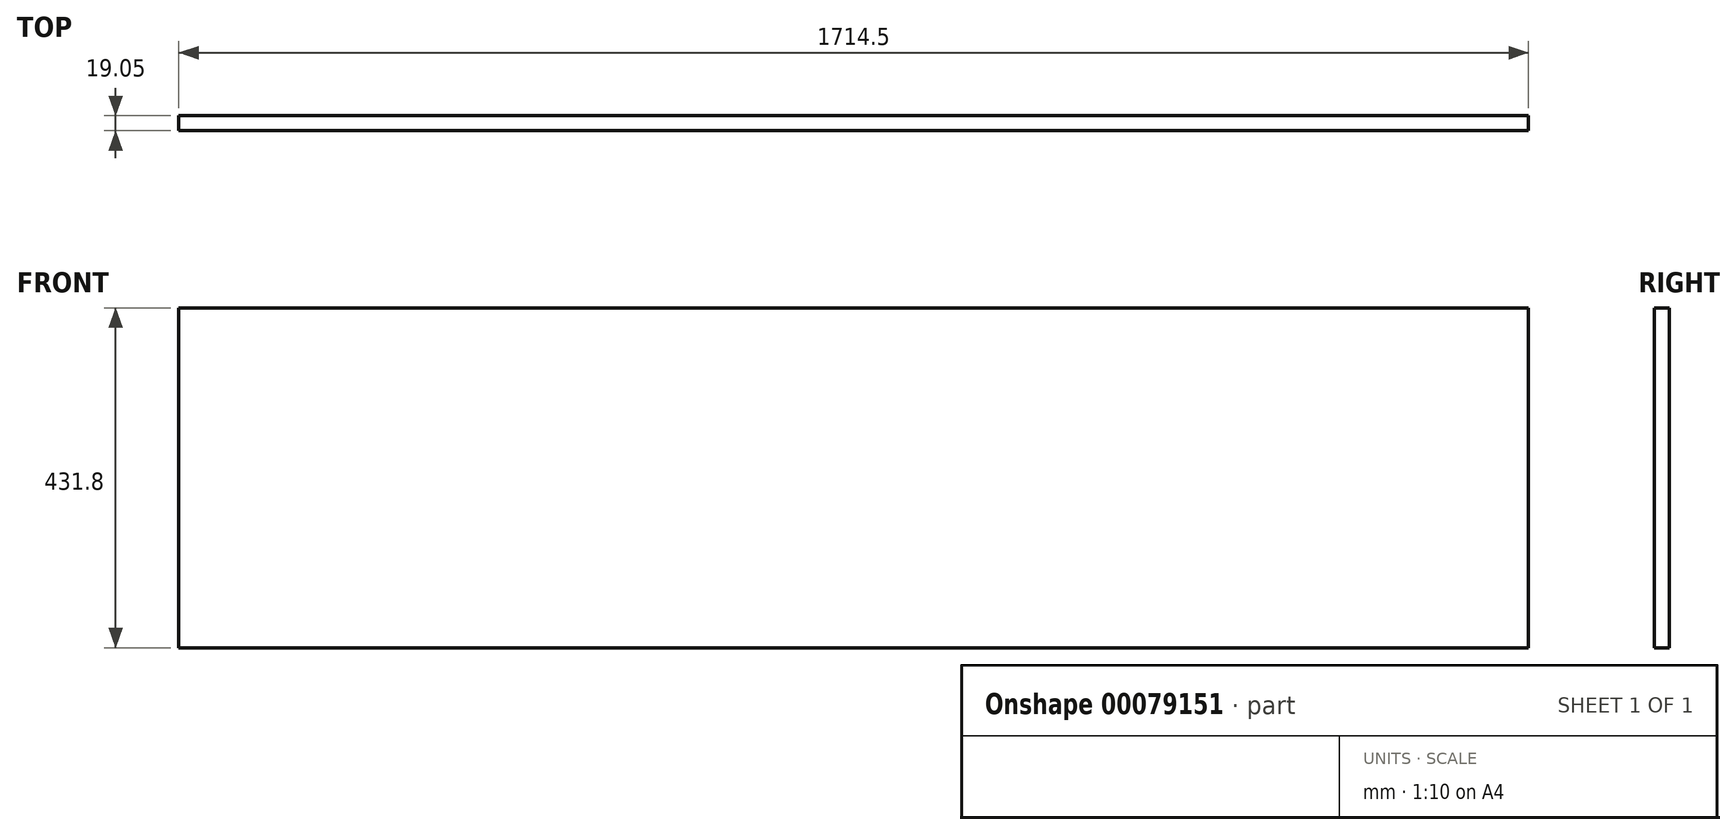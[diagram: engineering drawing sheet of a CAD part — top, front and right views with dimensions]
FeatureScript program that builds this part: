
annotation { "Feature Type Name" : "Feature", "Feature Type Description" : "" }
export const myFeature = defineFeature(function(context is Context, id is Id, definition is map)
    precondition{}
    {
        {
            var Q0;
            Q0=qCreatedBy(makeId("Front.planeOp"),FACE);
            var sketch = newSketch(context, id + "F0", { "sketchPlane" : qUnion([Q0])});
            skLineSegment(sketch, "E0.bottom", {"start": v(1284.35, 1245.88) * mm, "end": v(-430.15, 1245.88) * mm});
            skLineSegment(sketch, "E0.top", {"start": v(1284.35, 814.08) * mm, "end": v(-430.15, 814.08) * mm});
            skLineSegment(sketch, "E0.left", {"start": v(1284.35, 1245.88) * mm, "end": v(1284.35, 814.08) * mm});
            skLineSegment(sketch, "E0.right", {"start": v(-430.15, 1245.88) * mm, "end": v(-430.15, 814.08) * mm});
            skSolve(sketch);
        }
        {
            var Q0;
            Q0=makeQuery(id+"F0.imprint","IMPRINT",FACE,{"disambiguationData":[TD([[makeQuery(id+"F0.imprint","IMPRINT",EDGE,{"derivedFrom":sQuery(id+"F0.wireOp",EDGE,"E0.bottom")}),1.0]])]});
            extrude(context, id + "F1", {"entities" : qUnion([Q0]), "depth" : 19.05 * mm});
        }
    });
